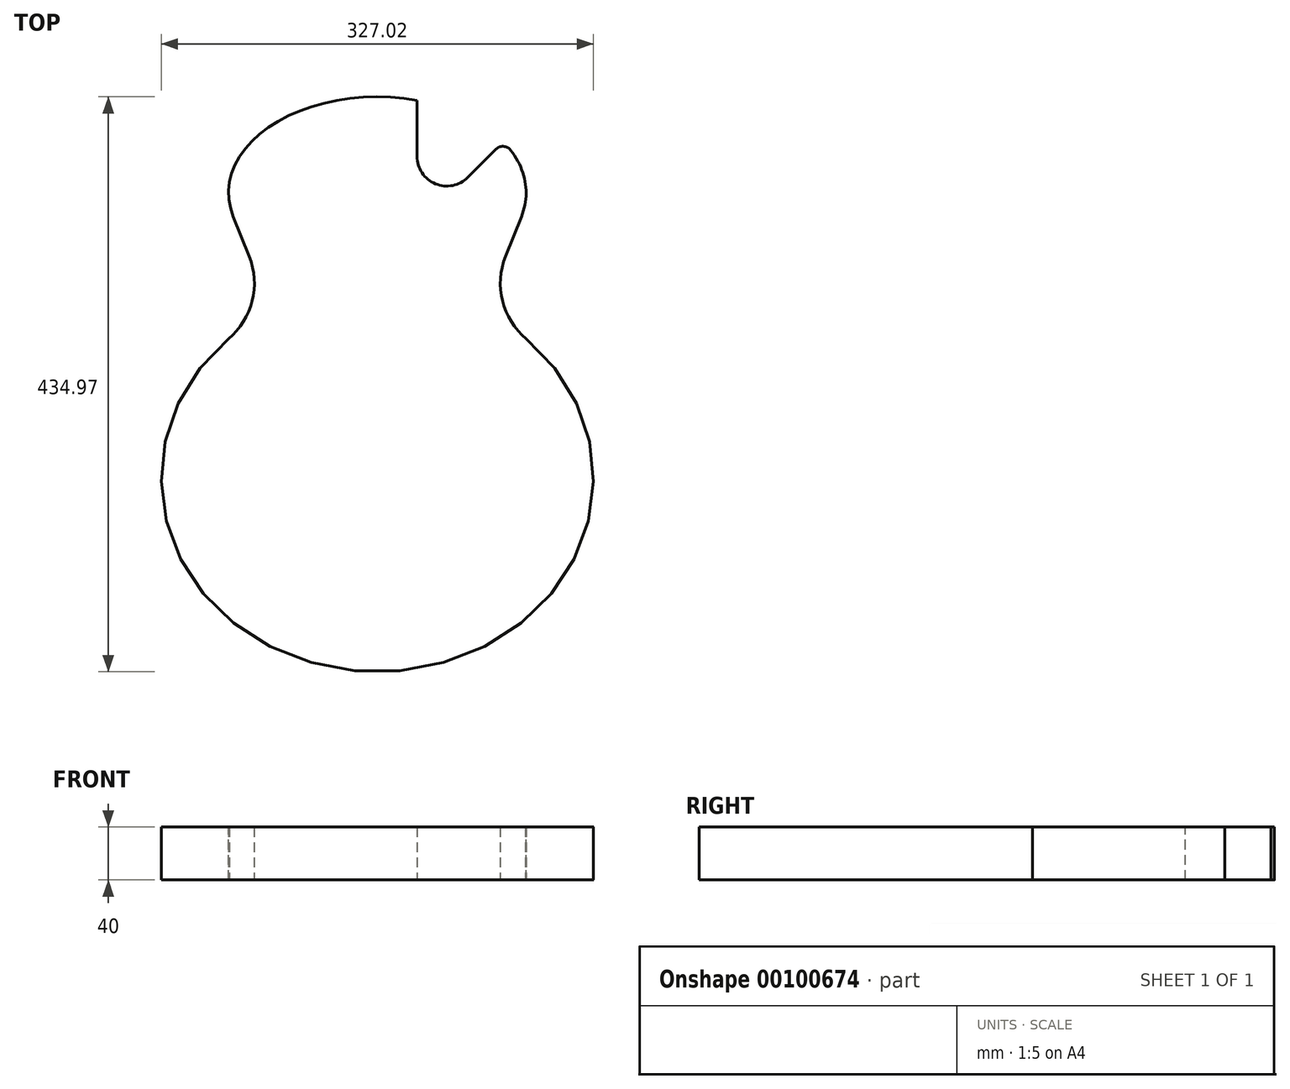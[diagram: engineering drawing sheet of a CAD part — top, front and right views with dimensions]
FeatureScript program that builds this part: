
annotation { "Feature Type Name" : "Feature", "Feature Type Description" : "" }
export const myFeature = defineFeature(function(context is Context, id is Id, definition is map)
    precondition{}
    {
        {
            var Q0;
            Q0=qCreatedBy(makeId("Top.planeOp"),FACE);
            var sketch = newSketch(context, id + "F0", { "sketchPlane" : qUnion([Q0]), "disableImprinting" : false});
            skEllipticalArc(sketch, "E0", {});
            skEllipticalArc(sketch, "E1", {});
            skLineSegment(sketch, "E2", {"start": v(0, 0) * mm, "end": v(0, 434.98) * mm, "construction": true});
            skLineSegment(sketch, "E3", {"start": v(-244.22, 0) * mm, "end": v(-244.22, 277.4) * mm, "construction": true});
            skLineSegment(sketch, "E4", {"start": v(-244.22, 277.4) * mm, "end": v(0, 277.4) * mm, "construction": true});
            skLineSegment(sketch, "E5", {"start": v(-82.17, 277.4) * mm, "end": v(-111.98, 252.4) * mm, "construction": true});
            skLineSegment(sketch, "E6", {"start": v(-96.94, 314.36) * mm, "end": v(-108.95, 344.4) * mm});
            skArc(sketch, "E7", {"start": v(-112.66, 251.82) * mm, "mid": v(-94.67, 280.54) * mm, "end": v(-96.94, 314.36) * mm});
            skEllipticalArc(sketch, "E8.MirrorCS", {});
            skLineSegment(sketch, "E9.MirrorCS", {"start": v(96.94, 314.36) * mm, "end": v(108.95, 344.4) * mm});
            skArc(sketch, "E10.MirrorCS", {"start": v(112.66, 251.82) * mm, "mid": v(94.67, 280.54) * mm, "end": v(96.94, 314.36) * mm});
            skEllipticalArc(sketch, "E11.MirrorCS", {});
            skPoint(sketch, "E12.orphan", {"position": v(113.63, 356.12) * mm});
            skPoint(sketch, "E13.orphan", {"position": v(-113.63, 356.12) * mm});
            skLineSegment(sketch, "E14", {"start": v(-112.66, 251.82) * mm, "end": v(-111.98, 252.4) * mm});
            skLineSegment(sketch, "E15", {"start": v(111.98, 252.4) * mm, "end": v(112.66, 251.82) * mm});
            skLineSegment(sketch, "E16", {"start": v(-125.15, 434.98) * mm, "end": v(125.15, 434.98) * mm, "construction": true});
            const initialGuessF0  = {"E0": [0, 0.146, 0, -1, 0.146, 0.1635125, 3.8959392904465506, 6.283185307179586], "E1": [0, 0.362475, -1, 0, 0.1125, 0.0725, 4.71238898038469, 0.2520546479388617], "E8.MirrorCS": [0, 0.362475, 1, 0, 0.1125, 0.0725, 6.031130659240725, 1.5707963267948966], "E11.MirrorCS": [0, 0.146, 0, -1, 0.146, 0.1635125, 6.283185307179586, 2.387246016733036]};
            skSetInitialGuess(sketch, initialGuessF0);
            skSolve(sketch);
        }
        {
            var Q0;
            Q0=qSketchRegion(id+"F0",true);
            extrude(context, id + "F1", {"entities" : qUnion([Q0]), "depth" : 40 * mm});
        }
        {
            var Q0;
            Q0=makeQuery(id+"F1.opExtrude","CAP_FACE",FACE,{"disambiguationData":[OSD([sQuery(id+"F0.wireOp",EDGE,"E0"),sQuery(id+"F0.wireOp",EDGE,"E1"),sQuery(id+"F0.wireOp",EDGE,"E6"),sQuery(id+"F0.wireOp",EDGE,"E7"),sQuery(id+"F0.wireOp",EDGE,"E8.MirrorCS"),sQuery(id+"F0.wireOp",EDGE,"E9.MirrorCS"),sQuery(id+"F0.wireOp",EDGE,"E10.MirrorCS"),sQuery(id+"F0.wireOp",EDGE,"E11.MirrorCS"),sQuery(id+"F0.wireOp",EDGE,"E14"),sQuery(id+"F0.wireOp",EDGE,"E15")])],"isStart":false});
            var sketch = newSketch(context, id + "F2", { "sketchPlane" : qUnion([Q0])});
            skLineSegment(sketch, "E17", {"start": v(0, 434.98) * mm, "end": v(0, 369.98) * mm, "construction": true});
            skPoint(sketch, "E17.endSnap0", {"position": v(0, 434.98) * mm});
            skLineSegment(sketch, "E18.0", {"start": v(30, 434.98) * mm, "end": v(30, 389.98) * mm});
            skLineSegment(sketch, "E19", {"start": v(0, 434.98) * mm, "end": v(30, 434.98) * mm, "construction": true});
            skArc(sketch, "E20", {"start": v(30, 389.98) * mm, "mid": v(43.89, 369.19) * mm, "end": v(68.4, 374.07) * mm});
            skLineSegment(sketch, "E21", {"start": v(68.4, 374.07) * mm, "end": v(89.64, 395.3) * mm});
            skArc(sketch, "E22", {"start": v(100.9, 394.55) * mm, "mid": v(95.43, 397.47) * mm, "end": v(89.64, 395.3) * mm});
            skLineSegment(sketch, "E23", {"start": v(100.9, 394.55) * mm, "end": v(69.95, 434.98) * mm});
            skLineSegment(sketch, "E24", {"start": v(30, 434.98) * mm, "end": v(69.95, 434.98) * mm});
            skSolve(sketch);
        }
        {
            var Q0;
            Q0 = qSketchRegion(id + "F2", true);
            extrude(context, id + "F3", {"entities" : qUnion([Q0]), "operationType" : NewBodyOperationType.REMOVE, "endBound" : BoundingType.THROUGH_ALL, "oppositeDirection" : true, "depth" : 25 * mm});
        }
    });
